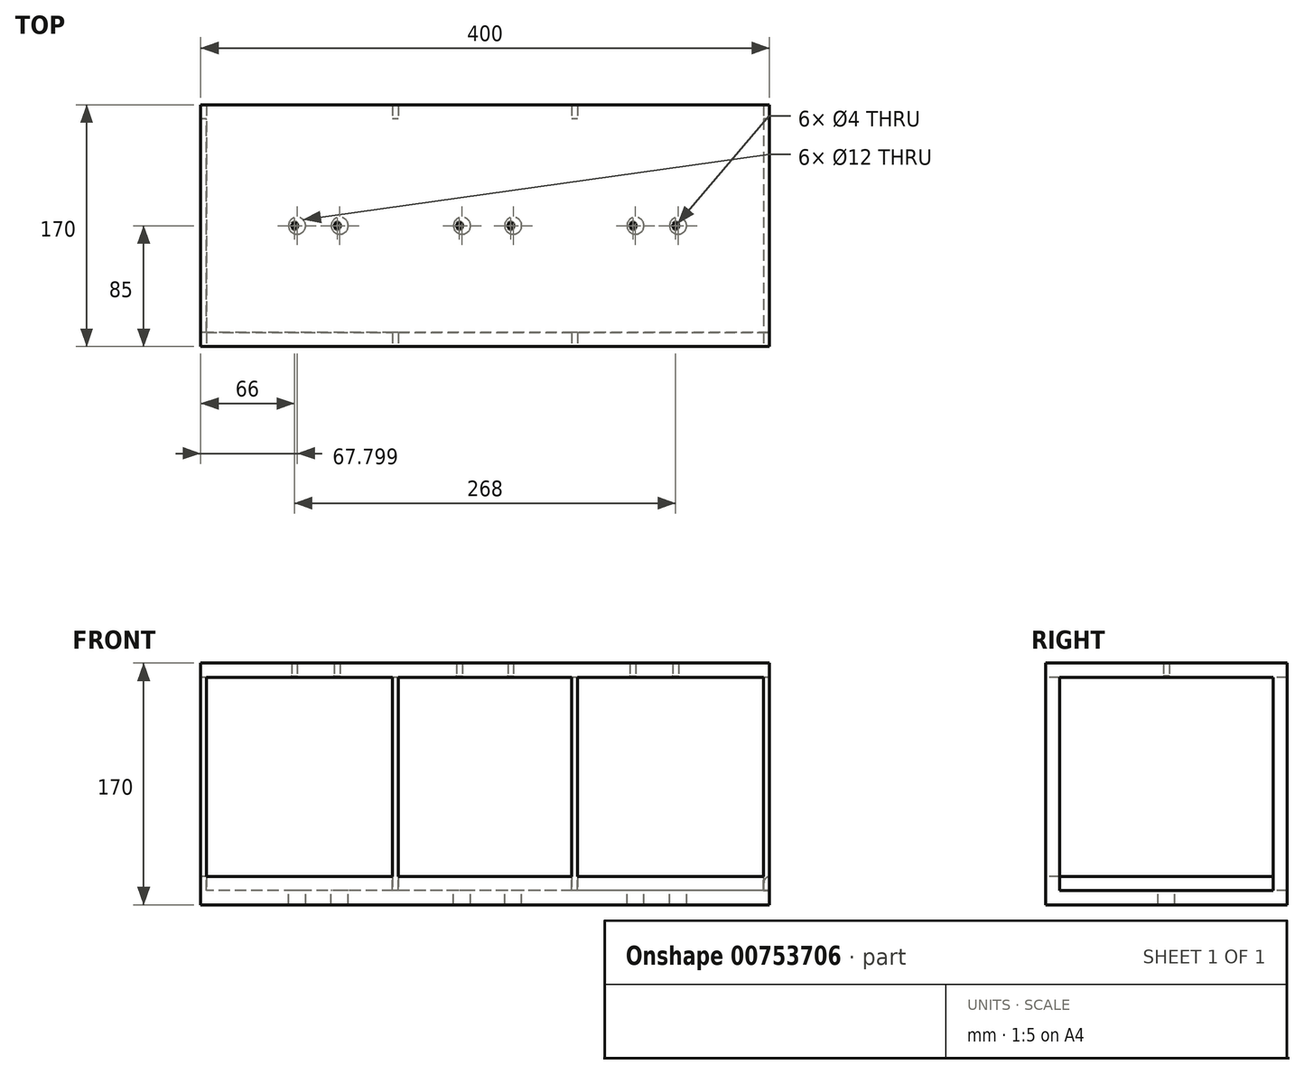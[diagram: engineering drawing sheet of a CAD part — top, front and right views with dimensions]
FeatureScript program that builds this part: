
annotation { "Feature Type Name" : "Feature", "Feature Type Description" : "" }
export const myFeature = defineFeature(function(context is Context, id is Id, definition is map)
    precondition{}
    {
        {
            var Q0;
            Q0=qCreatedBy(makeId("Right.planeOp"),FACE);
            var sketch = newSketch(context, id + "F0", { "sketchPlane" : qUnion([Q0])});
            skLineSegment(sketch, "E0.bottom", {"start": v(85, 85) * mm, "end": v(-85, 85) * mm});
            skLineSegment(sketch, "E0.top", {"start": v(85, -85) * mm, "end": v(-85, -85) * mm});
            skLineSegment(sketch, "E0.left", {"start": v(85, 85) * mm, "end": v(85, -85) * mm});
            skLineSegment(sketch, "E0.right", {"start": v(-85, 85) * mm, "end": v(-85, -85) * mm});
            skPoint(sketch, "E0.middle", {"position": v(0, 0) * mm});
            skSolve(sketch);
        }
        {
            var Q0;
            Q0 = qSketchRegion(id + "F0", true);
            extrude(context, id + "F1", {"entities" : qUnion([Q0]), "depth" : 400 * mm, "offsetDistance" : 25 * mm});
        }
        {
            var Q0;
            Q0=makeQuery(id+"F1.opExtrude","SWEPT_FACE",FACE,{"disambiguationData":[OSD([sQuery(id+"F0.wireOp",EDGE,"E0.right")])]});
            var sketch = newSketch(context, id + "F2", { "sketchPlane" : qUnion([Q0])});
            skLineSegment(sketch, "E1.bottom", {"start": v(4, 75) * mm, "end": v(135, 75) * mm});
            skLineSegment(sketch, "E1.top", {"start": v(4, -75) * mm, "end": v(135, -75) * mm});
            skLineSegment(sketch, "E1.left", {"start": v(4, 75) * mm, "end": v(4, -75) * mm});
            skLineSegment(sketch, "E1.right", {"start": v(135, 75) * mm, "end": v(135, -75) * mm});
            skPoint(sketch, "E1.middle", {"position": v(69.5, 0) * mm});
            skLineSegment(sketch, "E2.bottom", {"start": v(139, 75) * mm, "end": v(261, 75) * mm});
            skLineSegment(sketch, "E2.top", {"start": v(139, -75) * mm, "end": v(261, -75) * mm});
            skLineSegment(sketch, "E2.left", {"start": v(139, 75) * mm, "end": v(139, -75) * mm});
            skLineSegment(sketch, "E2.right", {"start": v(261, 75) * mm, "end": v(261, -75) * mm});
            skPoint(sketch, "E2.middle", {"position": v(200, 0) * mm});
            skLineSegment(sketch, "E3.bottom", {"start": v(265, 75) * mm, "end": v(396, 75) * mm});
            skLineSegment(sketch, "E3.top", {"start": v(265, -75) * mm, "end": v(396, -75) * mm});
            skLineSegment(sketch, "E3.left", {"start": v(265, 75) * mm, "end": v(265, -75) * mm});
            skLineSegment(sketch, "E3.right", {"start": v(396, 75) * mm, "end": v(396, -75) * mm});
            skPoint(sketch, "E3.middle", {"position": v(330.5, 0) * mm});
            skSolve(sketch);
        }
        {
            var Q0;
            Q0 = qSketchRegion(id + "F2", true);
            extrude(context, id + "F3", {"entities" : qUnion([Q0]), "operationType" : NewBodyOperationType.REMOVE, "oppositeDirection" : true, "depth" : 180 * mm, "offsetDistance" : 25 * mm});
        }
        {
            var Q0;
            Q0=makeQuery(id+"F1.opExtrude","CAP_FACE",FACE,{"disambiguationData":[OSD([sQuery(id+"F0.wireOp",EDGE,"E0.bottom"),sQuery(id+"F0.wireOp",EDGE,"E0.top"),sQuery(id+"F0.wireOp",EDGE,"E0.left"),sQuery(id+"F0.wireOp",EDGE,"E0.right")])],"isStart":true});
            var sketch = newSketch(context, id + "F4", { "sketchPlane" : qUnion([Q0])});
            skLineSegment(sketch, "E4.bottom", {"start": v(-75, 75) * mm, "end": v(75, 75) * mm});
            skLineSegment(sketch, "E4.top", {"start": v(-75, -75) * mm, "end": v(75, -75) * mm});
            skLineSegment(sketch, "E4.left", {"start": v(-75, 75) * mm, "end": v(-75, -75) * mm});
            skLineSegment(sketch, "E4.right", {"start": v(75, 75) * mm, "end": v(75, -75) * mm});
            skPoint(sketch, "E4.middle", {"position": v(0, 0) * mm});
            skSolve(sketch);
        }
        {
            var Q0;
            Q0 = qSketchRegion(id + "F4", true);
            extrude(context, id + "F5", {"entities" : qUnion([Q0]), "operationType" : NewBodyOperationType.REMOVE, "oppositeDirection" : true, "depth" : 400 * mm, "offsetDistance" : 25 * mm});
        }
        {
            var Q0;
            Q0=makeQuery(id+"F5.boolean.opBoolean","MERGE",FACE,{"derivedFrom":[makeQuery(id+"F3.boolean.opBoolean","COPY",FACE,{"derivedFrom":makeQuery(id+"F3.opExtrude","SWEPT_FACE",FACE,{"disambiguationData":[OSD([sQuery(id+"F2.wireOp",EDGE,"E1.bottom")])]})}),makeQuery(id+"F3.boolean.opBoolean","COPY",FACE,{"derivedFrom":makeQuery(id+"F3.opExtrude","SWEPT_FACE",FACE,{"disambiguationData":[OSD([sQuery(id+"F2.wireOp",EDGE,"E2.bottom")])]})}),makeQuery(id+"F3.boolean.opBoolean","COPY",FACE,{"derivedFrom":makeQuery(id+"F3.opExtrude","SWEPT_FACE",FACE,{"disambiguationData":[OSD([sQuery(id+"F2.wireOp",EDGE,"E3.bottom")])]})}),makeQuery(id+"F5.opExtrude","SWEPT_FACE",FACE,{"disambiguationData":[OSD([sQuery(id+"F4.wireOp",EDGE,"E4.bottom")])]})]});
            var sketch = newSketch(context, id + "F6", { "sketchPlane" : qUnion([Q0])});
            skPoint(sketch, "E5", {"position": v(66, 0) * mm});
            skPoint(sketch, "E6", {"position": v(182, 0) * mm});
            skPoint(sketch, "E7", {"position": v(334, 0) * mm});
            skPoint(sketch, "E8", {"position": v(96, 0) * mm});
            skPoint(sketch, "E9", {"position": v(218, 0) * mm});
            skPoint(sketch, "E10", {"position": v(304, 0) * mm});
            skSolve(sketch);
        }
        {
            var Q0;
            Q0=sQuery(id+"F6.wireOp",VERTEX,"E5");
            var Q1;
            Q1=sQuery(id+"F6.wireOp",VERTEX,"E6");
            var Q2;
            Q2=sQuery(id+"F6.wireOp",VERTEX,"E7");
            var Q3;
            Q3=sQuery(id+"F6.wireOp",VERTEX,"E8");
            var Q4;
            Q4=sQuery(id+"F6.wireOp",VERTEX,"E9");
            var Q5;
            Q5=sQuery(id+"F6.wireOp",VERTEX,"E10");
            var Q6;
            Q6=makeQuery(id+"F1.opExtrude","SWEPT_BODY",BODY,{"disambiguationData":[OSD([sQuery(id+"F0.wireOp",EDGE,"E0.bottom"),sQuery(id+"F0.wireOp",EDGE,"E0.top"),sQuery(id+"F0.wireOp",EDGE,"E0.left"),sQuery(id+"F0.wireOp",EDGE,"E0.right")])]});
            hole(context, id + "F7", {"style" : HoleStyle.C_SINK, "endStyle" : HoleEndStyle.THROUGH, "holeDiameter" : 4 * mm, "cSinkDiameter" : 6 * mm, "cSinkAngle" : 90 * degree, "majorDiameter" : 5 * mm, "isTappedThrough" : true, "tappedDepth" : 12 * mm, "tapClearance" : 3, "locations" : qUnion([Q0, Q1, Q2, Q3, Q4, Q5]), "scope" : qUnion([Q6])});
        }
        {
            var Q0;
            Q0=makeQuery(id+"F1.opExtrude","SWEPT_FACE",FACE,{"disambiguationData":[OSD([sQuery(id+"F0.wireOp",EDGE,"E0.right")])]});
            var sketch = newSketch(context, id + "F8", { "sketchPlane" : qUnion([Q0])});
            skLineSegment(sketch, "E11.bottom", {"start": v(4, -65) * mm, "end": v(396, -65) * mm});
            skLineSegment(sketch, "E11.top", {"start": v(4, -75) * mm, "end": v(396, -75) * mm});
            skLineSegment(sketch, "E11.left", {"start": v(4, -65) * mm, "end": v(4, -75) * mm});
            skLineSegment(sketch, "E11.right", {"start": v(396, -65) * mm, "end": v(396, -75) * mm});
            skSolve(sketch);
        }
        {
            var Q0;
            Q0 = qSketchRegion(id + "F8", true);
            extrude(context, id + "F9", {"entities" : qUnion([Q0]), "oppositeDirection" : true, "depth" : 10 * mm, "offsetDistance" : 25 * mm});
        }
        {
            var Q0;
            Q0=makeQuery(id+"F1.opExtrude","CAP_FACE",FACE,{"disambiguationData":[OSD([sQuery(id+"F0.wireOp",EDGE,"E0.bottom"),sQuery(id+"F0.wireOp",EDGE,"E0.top"),sQuery(id+"F0.wireOp",EDGE,"E0.left"),sQuery(id+"F0.wireOp",EDGE,"E0.right")])],"isStart":false});
            var sketch = newSketch(context, id + "F10", { "sketchPlane" : qUnion([Q0])});
            skLineSegment(sketch, "E12.bottom", {"start": v(-75, -65) * mm, "end": v(75, -65) * mm});
            skLineSegment(sketch, "E12.top", {"start": v(-75, -75) * mm, "end": v(75, -75) * mm});
            skLineSegment(sketch, "E12.left", {"start": v(-75, -65) * mm, "end": v(-75, -75) * mm});
            skLineSegment(sketch, "E12.right", {"start": v(75, -65) * mm, "end": v(75, -75) * mm});
            skSolve(sketch);
        }
        {
            var Q0;
            Q0 = qSketchRegion(id + "F10", true);
            extrude(context, id + "F11", {"entities" : qUnion([Q0]), "oppositeDirection" : true, "depth" : 4 * mm, "offsetDistance" : 25 * mm});
        }
        {
            var Q0;
            Q0=makeQuery(id+"F1.opExtrude","CAP_FACE",FACE,{"disambiguationData":[OSD([sQuery(id+"F0.wireOp",EDGE,"E0.bottom"),sQuery(id+"F0.wireOp",EDGE,"E0.top"),sQuery(id+"F0.wireOp",EDGE,"E0.left"),sQuery(id+"F0.wireOp",EDGE,"E0.right")])],"isStart":true});
            var sketch = newSketch(context, id + "F12", { "sketchPlane" : qUnion([Q0])});
            skLineSegment(sketch, "E13.bottom", {"start": v(75, -65) * mm, "end": v(-75, -65) * mm});
            skLineSegment(sketch, "E13.top", {"start": v(75, -75) * mm, "end": v(-75, -75) * mm});
            skLineSegment(sketch, "E13.left", {"start": v(75, -65) * mm, "end": v(75, -75) * mm});
            skLineSegment(sketch, "E13.right", {"start": v(-75, -65) * mm, "end": v(-75, -75) * mm});
            skSolve(sketch);
        }
        {
            var Q0;
            Q0 = qSketchRegion(id + "F12", true);
            extrude(context, id + "F13", {"entities" : qUnion([Q0]), "operationType" : NewBodyOperationType.ADD, "oppositeDirection" : true, "depth" : 4 * mm, "offsetDistance" : 25 * mm});
        }
        {
            var Q0;
            Q0=makeQuery(id+"F9.opExtrude","CAP_EDGE",EDGE,{"disambiguationData":[OSD([sQuery(id+"F8.wireOp",EDGE,"E11.bottom")])],"isStart":false});
            var Q1;
            Q1=makeQuery(id+"F11.opExtrude","CAP_EDGE",EDGE,{"disambiguationData":[OSD([sQuery(id+"F10.wireOp",EDGE,"E12.bottom")])],"isStart":false});
            var Q2;
            Q2=makeQuery(id+"F13.opExtrude","CAP_EDGE",EDGE,{"disambiguationData":[OSD([sQuery(id+"F12.wireOp",EDGE,"E13.bottom")])],"isStart":false});
            var Q3;
            Q3=makeQuery(id+"F5.boolean.opBoolean","INTERSECT",EDGE,{"derivedFrom":[makeQuery(id+"F3.boolean.opBoolean","COPY",FACE,{"derivedFrom":makeQuery(id+"F3.opExtrude","SWEPT_FACE",FACE,{"disambiguationData":[OSD([sQuery(id+"F2.wireOp",EDGE,"E1.left")])]})}),makeQuery(id+"F5.opExtrude","SWEPT_FACE",FACE,{"disambiguationData":[OSD([sQuery(id+"F4.wireOp",EDGE,"E4.right")])]})]});
            var Q4;
            Q4=makeQuery(id+"F5.boolean.opBoolean","INTERSECT",EDGE,{"derivedFrom":[makeQuery(id+"F3.boolean.opBoolean","COPY",FACE,{"derivedFrom":makeQuery(id+"F3.opExtrude","SWEPT_FACE",FACE,{"disambiguationData":[OSD([sQuery(id+"F2.wireOp",EDGE,"E3.right")])]})}),makeQuery(id+"F5.opExtrude","SWEPT_FACE",FACE,{"disambiguationData":[OSD([sQuery(id+"F4.wireOp",EDGE,"E4.right")])]})]});
            var Q5;
            Q5=makeQuery(id+"F5.boolean.opBoolean","INTERSECT",EDGE,{"derivedFrom":[makeQuery(id+"F3.boolean.opBoolean","COPY",FACE,{"derivedFrom":makeQuery(id+"F3.opExtrude","SWEPT_FACE",FACE,{"disambiguationData":[OSD([sQuery(id+"F2.wireOp",EDGE,"E2.right")])]})}),makeQuery(id+"F5.opExtrude","SWEPT_FACE",FACE,{"disambiguationData":[OSD([sQuery(id+"F4.wireOp",EDGE,"E4.right")])]})]});
            var Q6;
            Q6=makeQuery(id+"F5.boolean.opBoolean","INTERSECT",EDGE,{"derivedFrom":[makeQuery(id+"F3.boolean.opBoolean","COPY",FACE,{"derivedFrom":makeQuery(id+"F3.opExtrude","SWEPT_FACE",FACE,{"disambiguationData":[OSD([sQuery(id+"F2.wireOp",EDGE,"E3.left")])]})}),makeQuery(id+"F5.opExtrude","SWEPT_FACE",FACE,{"disambiguationData":[OSD([sQuery(id+"F4.wireOp",EDGE,"E4.right")])]})]});
            var Q7;
            Q7=makeQuery(id+"F5.boolean.opBoolean","INTERSECT",EDGE,{"derivedFrom":[makeQuery(id+"F3.boolean.opBoolean","COPY",FACE,{"derivedFrom":makeQuery(id+"F3.opExtrude","SWEPT_FACE",FACE,{"disambiguationData":[OSD([sQuery(id+"F2.wireOp",EDGE,"E1.right")])]})}),makeQuery(id+"F5.opExtrude","SWEPT_FACE",FACE,{"disambiguationData":[OSD([sQuery(id+"F4.wireOp",EDGE,"E4.right")])]})]});
            var Q8;
            Q8=makeQuery(id+"F5.boolean.opBoolean","INTERSECT",EDGE,{"derivedFrom":[makeQuery(id+"F3.boolean.opBoolean","COPY",FACE,{"derivedFrom":makeQuery(id+"F3.opExtrude","SWEPT_FACE",FACE,{"disambiguationData":[OSD([sQuery(id+"F2.wireOp",EDGE,"E2.left")])]})}),makeQuery(id+"F5.opExtrude","SWEPT_FACE",FACE,{"disambiguationData":[OSD([sQuery(id+"F4.wireOp",EDGE,"E4.right")])]})]});
            var Q9;
            Q9=makeQuery(id+"F5.boolean.opBoolean","INTERSECT",EDGE,{"derivedFrom":[makeQuery(id+"F3.boolean.opBoolean","COPY",FACE,{"derivedFrom":makeQuery(id+"F3.opExtrude","SWEPT_FACE",FACE,{"disambiguationData":[OSD([sQuery(id+"F2.wireOp",EDGE,"E3.right")])]})}),makeQuery(id+"F5.opExtrude","SWEPT_FACE",FACE,{"disambiguationData":[OSD([sQuery(id+"F4.wireOp",EDGE,"E4.left")])]})]});
            var Q10;
            Q10=makeQuery(id+"F5.boolean.opBoolean","INTERSECT",EDGE,{"derivedFrom":[makeQuery(id+"F3.boolean.opBoolean","COPY",FACE,{"derivedFrom":makeQuery(id+"F3.opExtrude","SWEPT_FACE",FACE,{"disambiguationData":[OSD([sQuery(id+"F2.wireOp",EDGE,"E3.left")])]})}),makeQuery(id+"F5.opExtrude","SWEPT_FACE",FACE,{"disambiguationData":[OSD([sQuery(id+"F4.wireOp",EDGE,"E4.left")])]})]});
            var Q11;
            Q11=makeQuery(id+"F5.boolean.opBoolean","INTERSECT",EDGE,{"derivedFrom":[makeQuery(id+"F3.boolean.opBoolean","COPY",FACE,{"derivedFrom":makeQuery(id+"F3.opExtrude","SWEPT_FACE",FACE,{"disambiguationData":[OSD([sQuery(id+"F2.wireOp",EDGE,"E2.right")])]})}),makeQuery(id+"F5.opExtrude","SWEPT_FACE",FACE,{"disambiguationData":[OSD([sQuery(id+"F4.wireOp",EDGE,"E4.left")])]})]});
            var Q12;
            Q12=makeQuery(id+"F5.boolean.opBoolean","INTERSECT",EDGE,{"derivedFrom":[makeQuery(id+"F3.boolean.opBoolean","COPY",FACE,{"derivedFrom":makeQuery(id+"F3.opExtrude","SWEPT_FACE",FACE,{"disambiguationData":[OSD([sQuery(id+"F2.wireOp",EDGE,"E2.left")])]})}),makeQuery(id+"F5.opExtrude","SWEPT_FACE",FACE,{"disambiguationData":[OSD([sQuery(id+"F4.wireOp",EDGE,"E4.left")])]})]});
            var Q13;
            Q13=makeQuery(id+"F5.boolean.opBoolean","INTERSECT",EDGE,{"derivedFrom":[makeQuery(id+"F3.boolean.opBoolean","COPY",FACE,{"derivedFrom":makeQuery(id+"F3.opExtrude","SWEPT_FACE",FACE,{"disambiguationData":[OSD([sQuery(id+"F2.wireOp",EDGE,"E1.right")])]})}),makeQuery(id+"F5.opExtrude","SWEPT_FACE",FACE,{"disambiguationData":[OSD([sQuery(id+"F4.wireOp",EDGE,"E4.left")])]})]});
            var Q14;
            Q14=makeQuery(id+"F5.boolean.opBoolean","INTERSECT",EDGE,{"derivedFrom":[makeQuery(id+"F3.boolean.opBoolean","COPY",FACE,{"derivedFrom":makeQuery(id+"F3.opExtrude","SWEPT_FACE",FACE,{"disambiguationData":[OSD([sQuery(id+"F2.wireOp",EDGE,"E1.left")])]})}),makeQuery(id+"F5.opExtrude","SWEPT_FACE",FACE,{"disambiguationData":[OSD([sQuery(id+"F4.wireOp",EDGE,"E4.left")])]})]});
            fillet(context, id + "F14", {"entities" : qUnion([Q0, Q1, Q2, Q3, Q4, Q5, Q6, Q7, Q8, Q9, Q10, Q11, Q12, Q13, Q14]), "radius" : 5 * mm, "tangentPropagation" : true, "allowEdgeOverflow" : false});
        }
        {
            var Q0;
            Q0=makeQuery(id+"F5.boolean.opBoolean","MERGE",FACE,{"derivedFrom":[makeQuery(id+"F3.boolean.opBoolean","COPY",FACE,{"derivedFrom":makeQuery(id+"F3.opExtrude","SWEPT_FACE",FACE,{"disambiguationData":[OSD([sQuery(id+"F2.wireOp",EDGE,"E1.top")])]})}),makeQuery(id+"F3.boolean.opBoolean","COPY",FACE,{"derivedFrom":makeQuery(id+"F3.opExtrude","SWEPT_FACE",FACE,{"disambiguationData":[OSD([sQuery(id+"F2.wireOp",EDGE,"E2.top")])]})}),makeQuery(id+"F3.boolean.opBoolean","COPY",FACE,{"derivedFrom":makeQuery(id+"F3.opExtrude","SWEPT_FACE",FACE,{"disambiguationData":[OSD([sQuery(id+"F2.wireOp",EDGE,"E3.top")])]})}),makeQuery(id+"F5.opExtrude","SWEPT_FACE",FACE,{"disambiguationData":[OSD([sQuery(id+"F4.wireOp",EDGE,"E4.top")])]})]});
            var sketch = newSketch(context, id + "F15", { "sketchPlane" : qUnion([Q0])});
            skPoint(sketch, "E14", {"position": v(67.8, 0) * mm});
            skPoint(sketch, "E15", {"position": v(183.8, 0) * mm});
            skPoint(sketch, "E16", {"position": v(335.8, 0) * mm});
            skPoint(sketch, "E17", {"position": v(97.8, 0) * mm});
            skPoint(sketch, "E18", {"position": v(219.8, 0) * mm});
            skPoint(sketch, "E19", {"position": v(305.8, 0) * mm});
            skSolve(sketch);
        }
        {
            var Q0;
            Q0=sQuery(id+"F15.wireOp",VERTEX,"E16");
            var Q1;
            Q1=sQuery(id+"F15.wireOp",VERTEX,"E19");
            var Q2;
            Q2=sQuery(id+"F15.wireOp",VERTEX,"E18");
            var Q3;
            Q3=sQuery(id+"F15.wireOp",VERTEX,"E15");
            var Q4;
            Q4=sQuery(id+"F15.wireOp",VERTEX,"E17");
            var Q5;
            Q5=sQuery(id+"F15.wireOp",VERTEX,"E14");
            var Q6;
            Q6=makeQuery(id+"F1.opExtrude","SWEPT_BODY",BODY,{"disambiguationData":[OSD([sQuery(id+"F0.wireOp",EDGE,"E0.bottom"),sQuery(id+"F0.wireOp",EDGE,"E0.top"),sQuery(id+"F0.wireOp",EDGE,"E0.left"),sQuery(id+"F0.wireOp",EDGE,"E0.right")])]});
            hole(context, id + "F16", {"style" : HoleStyle.SIMPLE, "endStyle" : HoleEndStyle.THROUGH, "holeDiameter" : 12 * mm, "majorDiameter" : 5 * mm, "isTappedThrough" : true, "tappedDepth" : 12 * mm, "tapClearance" : 3, "locations" : qUnion([Q0, Q1, Q2, Q3, Q4, Q5]), "scope" : qUnion([Q6])});
        }
    });
